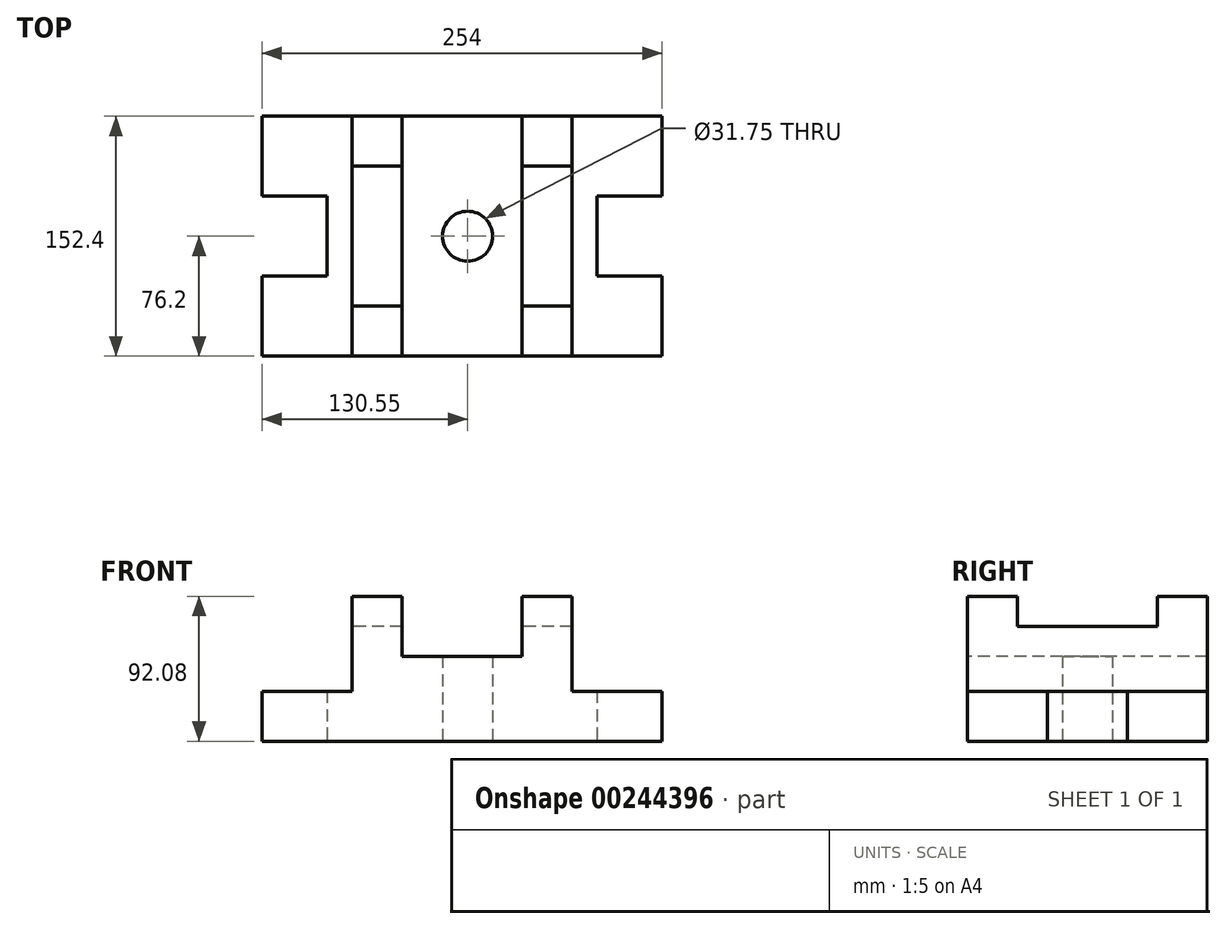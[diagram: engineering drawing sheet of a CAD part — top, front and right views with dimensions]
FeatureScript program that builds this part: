
annotation { "Feature Type Name" : "Feature", "Feature Type Description" : "" }
export const myFeature = defineFeature(function(context is Context, id is Id, definition is map)
    precondition{}
    {
        {
            var Q0;
            Q0=qCreatedBy(makeId("Top.planeOp"),FACE);
            var sketch = newSketch(context, id + "F0", { "sketchPlane" : qUnion([Q0])});
            skLineSegment(sketch, "E0", {"start": v(-130.55, -101.6) * mm, "end": v(123.45, -101.6) * mm});
            skLineSegment(sketch, "E1", {"start": v(123.45, -101.6) * mm, "end": v(123.45, -50.8) * mm});
            skLineSegment(sketch, "E2", {"start": v(123.45, -50.8) * mm, "end": v(82.18, -50.8) * mm});
            skLineSegment(sketch, "E3", {"start": v(82.18, 0) * mm, "end": v(123.45, 0) * mm});
            skLineSegment(sketch, "E4", {"start": v(82.18, 0) * mm, "end": v(82.18, -50.8) * mm});
            skLineSegment(sketch, "E5", {"start": v(123.45, 0) * mm, "end": v(123.45, 50.8) * mm});
            skLineSegment(sketch, "E6", {"start": v(123.45, 50.8) * mm, "end": v(-130.55, 50.8) * mm});
            skLineSegment(sketch, "E7", {"start": v(-130.55, 50.8) * mm, "end": v(-130.55, 0) * mm});
            skLineSegment(sketch, "E8", {"start": v(-130.55, 0) * mm, "end": v(-89.27, 0) * mm});
            skLineSegment(sketch, "E9", {"start": v(-89.27, 0) * mm, "end": v(-89.27, -50.8) * mm});
            skLineSegment(sketch, "E10", {"start": v(-89.27, -50.8) * mm, "end": v(-130.55, -50.8) * mm});
            skLineSegment(sketch, "E11", {"start": v(-130.55, -50.8) * mm, "end": v(-130.55, -101.6) * mm});
            skCircle(sketch, "E12", {"center": v(0, -25.4) * mm, "radius": 15.88 * mm});
            skLineSegment(sketch, "E13", {"start": v(-73.4, 50.8) * mm, "end": v(-73.4, -101.6) * mm});
            skLineSegment(sketch, "E14", {"start": v(66.3, 50.8) * mm, "end": v(66.3, -101.6) * mm});
            skLineSegment(sketch, "E15", {"start": v(-41.65, 50.8) * mm, "end": v(-41.65, -101.6) * mm});
            skLineSegment(sketch, "E16", {"start": v(34.55, 50.8) * mm, "end": v(34.55, -101.6) * mm});
            skLineSegment(sketch, "E17", {"start": v(34.55, 19.05) * mm, "end": v(66.3, 19.05) * mm});
            skLineSegment(sketch, "E18", {"start": v(66.3, -69.85) * mm, "end": v(34.55, -69.85) * mm});
            skLineSegment(sketch, "E19", {"start": v(-41.65, -69.85) * mm, "end": v(-73.4, -69.85) * mm});
            skLineSegment(sketch, "E20", {"start": v(-73.4, 19.05) * mm, "end": v(-41.65, 19.05) * mm});
            skSolve(sketch);
        }
        {
            var Q0;
            {var subQ0=sQuery(id+"F0.wireOp",EDGE,"E7");Q0=makeQuery(id+"F0.imprint","IMPRINT",FACE,{"disambiguationData":[TD([[makeQuery(id+"F0.imprint","IMPRINT",EDGE,{"derivedFrom":subQ0}),1.0]])]});}
            var Q1;
            {var subQ5=sQuery(id+"F0.wireOp",EDGE,"E1");Q1=makeQuery(id+"F0.imprint","IMPRINT",FACE,{"disambiguationData":[TD([[makeQuery(id+"F0.imprint","IMPRINT",EDGE,{"derivedFrom":subQ5}),1.0]])]});}
            extrude(context, id + "F1", {"entities" : qUnion([Q0, Q1]), "depth" : 31.75 * mm});
        }
        {
            var Q0;
            {var subQ5=sQuery(id+"F0.wireOp",EDGE,"E20");Q0=makeQuery(id+"F0.imprint","IMPRINT",FACE,{"disambiguationData":[TD([[makeQuery(id+"F0.imprint","IMPRINT",EDGE,{"derivedFrom":subQ5}),1.0]])]});}
            var Q1;
            {var subQ5=sQuery(id+"F0.wireOp",EDGE,"E19");Q1=makeQuery(id+"F0.imprint","IMPRINT",FACE,{"disambiguationData":[TD([[makeQuery(id+"F0.imprint","IMPRINT",EDGE,{"derivedFrom":subQ5}),1.0]])]});}
            var Q2;
            {var subQ5=sQuery(id+"F0.wireOp",EDGE,"E18");Q2=makeQuery(id+"F0.imprint","IMPRINT",FACE,{"disambiguationData":[TD([[makeQuery(id+"F0.imprint","IMPRINT",EDGE,{"derivedFrom":subQ5}),1.0]])]});}
            var Q3;
            {var subQ5=sQuery(id+"F0.wireOp",EDGE,"E17");Q3=makeQuery(id+"F0.imprint","IMPRINT",FACE,{"disambiguationData":[TD([[makeQuery(id+"F0.imprint","IMPRINT",EDGE,{"derivedFrom":subQ5}),1.0]])]});}
            extrude(context, id + "F2", {"entities" : qUnion([Q0, Q1, Q2, Q3]), "operationType" : NewBodyOperationType.ADD, "depth" : 92.07 * mm});
        }
        {
            var Q0;
            {var subQ0=sQuery(id+"F0.wireOp",EDGE,"E19");Q0=makeQuery(id+"F0.imprint","IMPRINT",FACE,{"disambiguationData":[TD([[makeQuery(id+"F0.imprint","IMPRINT",EDGE,{"derivedFrom":subQ0}),-1.0]])]});}
            var Q1;
            {var subQ0=sQuery(id+"F0.wireOp",EDGE,"E17");Q1=makeQuery(id+"F0.imprint","IMPRINT",FACE,{"disambiguationData":[TD([[makeQuery(id+"F0.imprint","IMPRINT",EDGE,{"derivedFrom":subQ0}),-1.0]])]});}
            extrude(context, id + "F3", {"entities" : qUnion([Q0, Q1]), "operationType" : NewBodyOperationType.ADD, "depth" : 73.02 * mm});
        }
        {
            var Q0;
            Q0=makeQuery(id+"F0.imprint","IMPRINT",FACE,{"disambiguationData":[TD([[makeQuery(id+"F0.imprint","IMPRINT",EDGE,{"derivedFrom":sQuery(id+"F0.wireOp",EDGE,"E12")}),-1.0]])]});
            extrude(context, id + "F4", {"entities" : qUnion([Q0]), "operationType" : NewBodyOperationType.ADD, "depth" : 53.97 * mm});
        }
    });
